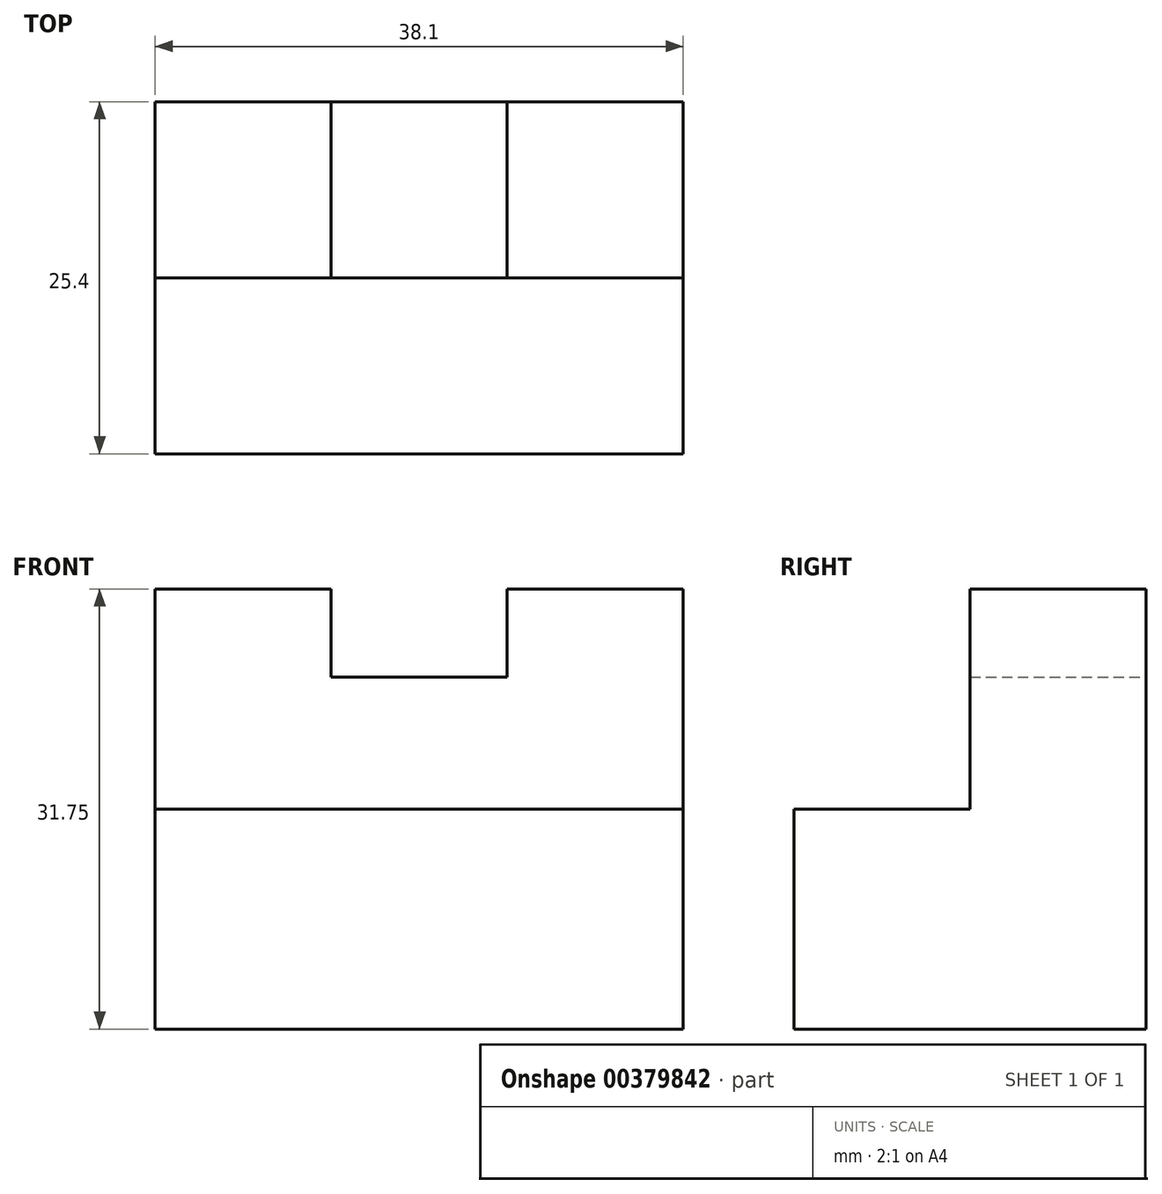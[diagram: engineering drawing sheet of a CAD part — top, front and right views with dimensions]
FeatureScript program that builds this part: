
annotation { "Feature Type Name" : "Feature", "Feature Type Description" : "" }
export const myFeature = defineFeature(function(context is Context, id is Id, definition is map)
    precondition{}
    {
        {
            var Q0;
            Q0=qCreatedBy(makeId("Front.planeOp"),FACE);
            var sketch = newSketch(context, id + "F0", { "sketchPlane" : qUnion([Q0])});
            skLineSegment(sketch, "E0", {"start": v(0, 0) * mm, "end": v(38.1, 0) * mm});
            skLineSegment(sketch, "E1", {"start": v(0, 0) * mm, "end": v(0, 0) * mm});
            skLineSegment(sketch, "E2", {"start": v(0, 0) * mm, "end": v(0, 31.75) * mm});
            skLineSegment(sketch, "E3", {"start": v(38.1, 0) * mm, "end": v(38.1, 31.75) * mm});
            skLineSegment(sketch, "E4", {"start": v(0, 31.75) * mm, "end": v(12.7, 31.75) * mm});
            skLineSegment(sketch, "E5", {"start": v(12.7, 31.75) * mm, "end": v(12.7, 25.4) * mm});
            skLineSegment(sketch, "E6", {"start": v(12.7, 25.4) * mm, "end": v(25.4, 25.4) * mm});
            skLineSegment(sketch, "E7", {"start": v(25.4, 25.4) * mm, "end": v(25.4, 31.75) * mm});
            skLineSegment(sketch, "E8", {"start": v(25.4, 31.75) * mm, "end": v(38.1, 31.75) * mm});
            skSolve(sketch);
        }
        {
            var Q0;
            Q0=makeQuery(id+"F0.imprint","IMPRINT",FACE,{"disambiguationData":[TD([[makeQuery(id+"F0.imprint","IMPRINT",EDGE,{"derivedFrom":sQuery(id+"F0.wireOp",EDGE,"E0")}),1.0]])]});
            extrude(context, id + "F1", {"entities" : qUnion([Q0]), "depth" : 25.4 * mm});
        }
        {
            var Q0;
            Q0=makeQuery(id+"F1.opExtrude","CAP_FACE",FACE,{"disambiguationData":[OSD([sQuery(id+"F0.wireOp",EDGE,"E0"),sQuery(id+"F0.wireOp",EDGE,"E2"),sQuery(id+"F0.wireOp",EDGE,"E3"),sQuery(id+"F0.wireOp",EDGE,"E4"),sQuery(id+"F0.wireOp",EDGE,"E5"),sQuery(id+"F0.wireOp",EDGE,"E6"),sQuery(id+"F0.wireOp",EDGE,"E7"),sQuery(id+"F0.wireOp",EDGE,"E8")])],"isStart":false});
            var sketch = newSketch(context, id + "F2", { "sketchPlane" : qUnion([Q0])});
            skLineSegment(sketch, "E9", {"start": v(0, 15.88) * mm, "end": v(38.1, 15.88) * mm});
            skSolve(sketch);
        }
        {
            var Q0;
            {var subQ1=sQuery(id+"F2.wireOp",EDGE,"E9");Q0=makeQuery(id+"F2.imprint","IMPRINT",FACE,{"disambiguationData":[TD([[makeQuery(id+"F2.imprint","IMPRINT",EDGE,{"derivedFrom":subQ1}),1.0]])]});}
            extrude(context, id + "F3", {"entities" : qUnion([Q0]), "operationType" : NewBodyOperationType.REMOVE, "oppositeDirection" : true, "depth" : 12.7 * mm});
        }
    });
